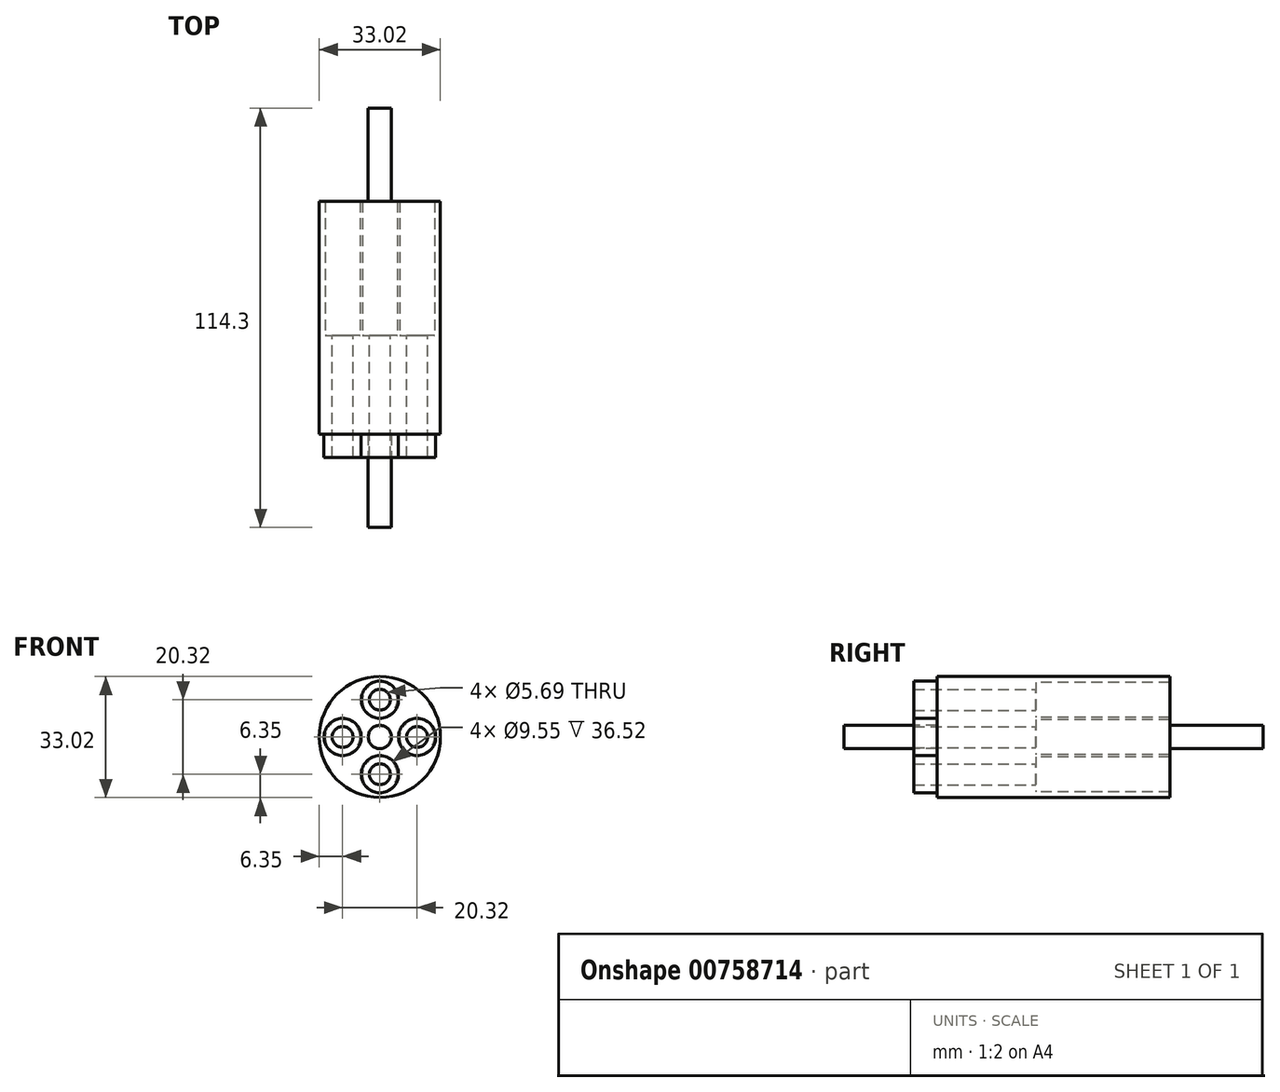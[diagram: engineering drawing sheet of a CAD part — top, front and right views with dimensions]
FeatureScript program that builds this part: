
annotation { "Feature Type Name" : "Feature", "Feature Type Description" : "" }
export const myFeature = defineFeature(function(context is Context, id is Id, definition is map)
    precondition{}
    {
        {
            var Q0;
            Q0=qCreatedBy(makeId("Front.planeOp"),FACE);
            var sketch = newSketch(context, id + "F0", { "sketchPlane" : qUnion([Q0])});
            skCircle(sketch, "E0", {"center": v(0, 0) * mm, "radius": 16.51 * mm});
            skLineSegment(sketch, "E1", {"start": v(0, 0) * mm, "end": v(0, 16.51) * mm});
            skLineSegment(sketch, "E2", {"start": v(0, 0) * mm, "end": v(16.51, 0) * mm});
            skLineSegment(sketch, "E3", {"start": v(0, 0) * mm, "end": v(0, -16.51) * mm});
            skLineSegment(sketch, "E4", {"start": v(0, 0) * mm, "end": v(-16.51, 0) * mm});
            skCircle(sketch, "E5", {"center": v(-10.16, 0) * mm, "radius": 2.84 * mm});
            skCircle(sketch, "E6", {"center": v(0, 10.16) * mm, "radius": 2.84 * mm});
            skCircle(sketch, "E7", {"center": v(10.16, 0) * mm, "radius": 2.84 * mm});
            skCircle(sketch, "E8", {"center": v(0, -10.16) * mm, "radius": 2.84 * mm});
            skLineSegment(sketch, "E9", {"start": v(0, -10.16) * mm, "end": v(0, 0) * mm});
            skLineSegment(sketch, "E10", {"start": v(0, 0) * mm, "end": v(10.16, 0) * mm});
            skLineSegment(sketch, "E11", {"start": v(0, 10.16) * mm, "end": v(0, 0) * mm});
            skLineSegment(sketch, "E12", {"start": v(0, 0) * mm, "end": v(-10.16, 0) * mm});
            skSolve(sketch);
        }
        {
            var Q0;
            {var subQ5=sQuery(id+"F0.wireOp",EDGE,"E1");var subQ6=sQuery(id+"F0.wireOp",EDGE,"E0");var subQ7=makeQuery(id+"F0.imprint","INTERSECT",VERTEX,{"derivedFrom":[subQ6,subQ5]});Q0=makeQuery(id+"F0.imprint","IMPRINT",FACE,{"disambiguationData":[TD([[makeQuery(id+"F0.imprint","IMPRINT",EDGE,{"disambiguationData":[TD([[subQ7,-1.0]])],"derivedFrom":subQ6}),1.0]])]});}
            var Q1;
            {var subQ5=sQuery(id+"F0.wireOp",EDGE,"E3");var subQ6=sQuery(id+"F0.wireOp",EDGE,"E0");var subQ7=makeQuery(id+"F0.imprint","INTERSECT",VERTEX,{"derivedFrom":[subQ6,subQ5]});Q1=makeQuery(id+"F0.imprint","IMPRINT",FACE,{"disambiguationData":[TD([[makeQuery(id+"F0.imprint","IMPRINT",EDGE,{"disambiguationData":[TD([[subQ7,1.0]])],"derivedFrom":subQ6}),1.0]])]});}
            var Q2;
            {var subQ1=sQuery(id+"F0.wireOp",EDGE,"E0");var subQ6=sQuery(id+"F0.wireOp",EDGE,"E2");var subQ10=makeQuery(id+"F0.imprint","INTERSECT",VERTEX,{"derivedFrom":[subQ1,subQ6]});Q2=makeQuery(id+"F0.imprint","IMPRINT",FACE,{"disambiguationData":[TD([[makeQuery(id+"F0.imprint","IMPRINT",EDGE,{"disambiguationData":[TD([[subQ10,1.0]])],"derivedFrom":subQ1}),1.0]])]});}
            var Q3;
            {var subQ1=sQuery(id+"F0.wireOp",EDGE,"E0");var subQ6=sQuery(id+"F0.wireOp",EDGE,"E1");var subQ10=makeQuery(id+"F0.imprint","INTERSECT",VERTEX,{"derivedFrom":[subQ1,subQ6]});Q3=makeQuery(id+"F0.imprint","IMPRINT",FACE,{"disambiguationData":[TD([[makeQuery(id+"F0.imprint","IMPRINT",EDGE,{"disambiguationData":[TD([[subQ10,1.0]])],"derivedFrom":subQ1}),1.0]])]});}
            extrude(context, id + "F1", {"entities" : qUnion([Q0, Q1, Q2, Q3]), "depth" : 63.5 * mm, "offsetDistance" : 25.4 * mm});
        }
        {
            var Q0;
            Q0=makeQuery(id+"F1.opExtrude","CAP_FACE",FACE,{"disambiguationData":[OSD([sQuery(id+"F0.wireOp",EDGE,"E0"),sQuery(id+"F0.wireOp",EDGE,"E5"),sQuery(id+"F0.wireOp",EDGE,"E6"),sQuery(id+"F0.wireOp",EDGE,"E7"),sQuery(id+"F0.wireOp",EDGE,"E8")])],"isStart":false});
            var sketch = newSketch(context, id + "F2", { "sketchPlane" : qUnion([Q0])});
            skLineSegment(sketch, "E13", {"start": v(0, 0) * mm, "end": v(0, 10.16) * mm});
            skLineSegment(sketch, "E14", {"start": v(0, 0) * mm, "end": v(10.16, 0) * mm});
            skLineSegment(sketch, "E15", {"start": v(0, 0) * mm, "end": v(0, -10.16) * mm});
            skLineSegment(sketch, "E16", {"start": v(0, 0) * mm, "end": v(-10.16, 0) * mm});
            skCircle(sketch, "E17", {"center": v(0, 10.16) * mm, "radius": 5.08 * mm});
            skCircle(sketch, "E18", {"center": v(10.16, 0) * mm, "radius": 5.08 * mm});
            skCircle(sketch, "E19", {"center": v(0, -10.16) * mm, "radius": 5.08 * mm});
            skCircle(sketch, "E20", {"center": v(-10.16, 0) * mm, "radius": 5.08 * mm});
            skSolve(sketch);
        }
        {
            var Q0;
            Q0=makeQuery(id+"F2.imprint","IMPRINT",FACE,{"disambiguationData":[TD([[makeQuery(id+"F2.imprint","IMPRINT",EDGE,{"derivedFrom":sQuery(id+"F2.wireOp",EDGE,"E17")}),1.0]])]});
            var Q1;
            Q1=makeQuery(id+"F2.imprint","IMPRINT",FACE,{"disambiguationData":[TD([[makeQuery(id+"F2.imprint","IMPRINT",EDGE,{"derivedFrom":sQuery(id+"F2.wireOp",EDGE,"E20")}),1.0]])]});
            var Q2;
            Q2=makeQuery(id+"F2.imprint","IMPRINT",FACE,{"disambiguationData":[TD([[makeQuery(id+"F2.imprint","IMPRINT",EDGE,{"derivedFrom":sQuery(id+"F2.wireOp",EDGE,"E19")}),1.0]])]});
            var Q3;
            Q3=makeQuery(id+"F2.imprint","IMPRINT",FACE,{"disambiguationData":[TD([[makeQuery(id+"F2.imprint","IMPRINT",EDGE,{"derivedFrom":sQuery(id+"F2.wireOp",EDGE,"E18")}),1.0]])]});
            extrude(context, id + "F3", {"entities" : qUnion([Q0, Q1, Q2, Q3]), "operationType" : NewBodyOperationType.ADD, "depth" : 6.35 * mm, "offsetDistance" : 25.4 * mm});
        }
        {
            var Q0;
            Q0=makeQuery(id+"F1.opExtrude","CAP_FACE",FACE,{"disambiguationData":[OSD([sQuery(id+"F0.wireOp",EDGE,"E0"),sQuery(id+"F0.wireOp",EDGE,"E5"),sQuery(id+"F0.wireOp",EDGE,"E6"),sQuery(id+"F0.wireOp",EDGE,"E7"),sQuery(id+"F0.wireOp",EDGE,"E8")])],"isStart":true});
            var sketch = newSketch(context, id + "F4", { "sketchPlane" : qUnion([Q0])});
            skCircle(sketch, "E21", {"center": v(0, 10.16) * mm, "radius": 4.78 * mm});
            skCircle(sketch, "E22", {"center": v(-10.16, 0) * mm, "radius": 4.78 * mm});
            skCircle(sketch, "E23", {"center": v(10.16, 0) * mm, "radius": 4.78 * mm});
            skCircle(sketch, "E24", {"center": v(0, -10.16) * mm, "radius": 4.78 * mm});
            skSolve(sketch);
        }
        {
            var Q0;
            Q0=qCreatedBy(makeId("Right.planeOp"),FACE);
            var sketch = newSketch(context, id + "F5", { "sketchPlane" : qUnion([Q0])});
            skLineSegment(sketch, "E25", {"start": v(0, 0) * mm, "end": v(-36.52, 0) * mm});
            skLineSegment(sketch, "E26", {"start": v(-47.12, 0) * mm, "end": v(-57.4, 0) * mm});
            skLineSegment(sketch, "E27", {"start": v(0, 0) * mm, "end": v(0, 26.66) * mm});
            skLineSegment(sketch, "E28", {"start": v(0, 26.66) * mm, "end": v(-57.4, 26.66) * mm});
            skLineSegment(sketch, "E29", {"start": v(0, 20.12) * mm, "end": v(-47.12, 20.12) * mm});
            skLineSegment(sketch, "E30", {"start": v(-44.7, 0) * mm, "end": v(-47.12, 0) * mm});
            skLineSegment(sketch, "E31", {"start": v(0, 31.17) * mm, "end": v(-44.7, 31.17) * mm});
            skLineSegment(sketch, "E32", {"start": v(-39.55, 0) * mm, "end": v(-44.7, 0) * mm});
            skLineSegment(sketch, "E33", {"start": v(0, -32.9) * mm, "end": v(-39.55, -32.9) * mm});
            skLineSegment(sketch, "E34", {"start": v(-36.52, 0) * mm, "end": v(-39.55, 0) * mm});
            skLineSegment(sketch, "E35", {"start": v(0, -40.42) * mm, "end": v(-36.52, -40.42) * mm});
            skSolve(sketch);
        }
        {
            var Q0;
            Q0=makeQuery(id+"F4.imprint","IMPRINT",FACE,{"disambiguationData":[TD([[makeQuery(id+"F4.imprint","IMPRINT",EDGE,{"derivedFrom":sQuery(id+"F4.wireOp",EDGE,"E22")}),1.0]])]});
            var Q1;
            Q1=makeQuery(id+"F4.imprint","IMPRINT",FACE,{"disambiguationData":[TD([[makeQuery(id+"F4.imprint","IMPRINT",EDGE,{"derivedFrom":sQuery(id+"F4.wireOp",EDGE,"E21")}),1.0]])]});
            var Q2;
            Q2=makeQuery(id+"F4.imprint","IMPRINT",FACE,{"disambiguationData":[TD([[makeQuery(id+"F4.imprint","IMPRINT",EDGE,{"derivedFrom":sQuery(id+"F4.wireOp",EDGE,"E23")}),1.0]])]});
            var Q3;
            Q3=makeQuery(id+"F4.imprint","IMPRINT",FACE,{"disambiguationData":[TD([[makeQuery(id+"F4.imprint","IMPRINT",EDGE,{"derivedFrom":sQuery(id+"F4.wireOp",EDGE,"E24")}),1.0]])]});
            var Q4;
            Q4=sQuery(id+"F5.wireOp",EDGE,"E35");
            sweep(context, id + "F6", {"operationType" : NewBodyOperationType.REMOVE, "profiles" : qUnion([Q0, Q1, Q2, Q3]), "path" : qUnion([Q4])});
        }
        {
            var Q0;
            Q0=makeQuery(id+"F1.opExtrude","CAP_FACE",FACE,{"disambiguationData":[OSD([sQuery(id+"F0.wireOp",EDGE,"E0"),sQuery(id+"F0.wireOp",EDGE,"E5"),sQuery(id+"F0.wireOp",EDGE,"E6"),sQuery(id+"F0.wireOp",EDGE,"E7"),sQuery(id+"F0.wireOp",EDGE,"E8")])],"isStart":true});
            var sketch = newSketch(context, id + "F7", { "sketchPlane" : qUnion([Q0])});
            skCircle(sketch, "E36", {"center": v(0, 0) * mm, "radius": 3.18 * mm});
            skSolve(sketch);
        }
        {
            var Q0;
            Q0=makeQuery(id+"F7.imprint","IMPRINT",FACE,{"disambiguationData":[TD([[makeQuery(id+"F7.imprint","IMPRINT",EDGE,{"derivedFrom":sQuery(id+"F7.wireOp",EDGE,"E36")}),1.0]])]});
            extrude(context, id + "F8", {"entities" : qUnion([Q0]), "operationType" : NewBodyOperationType.ADD, "depth" : 25.4 * mm, "offsetDistance" : 25.4 * mm, "hasSecondDirection" : true, "secondDirectionOppositeDirection" : true, "secondDirectionDepth" : 88.9 * mm});
        }
    });
